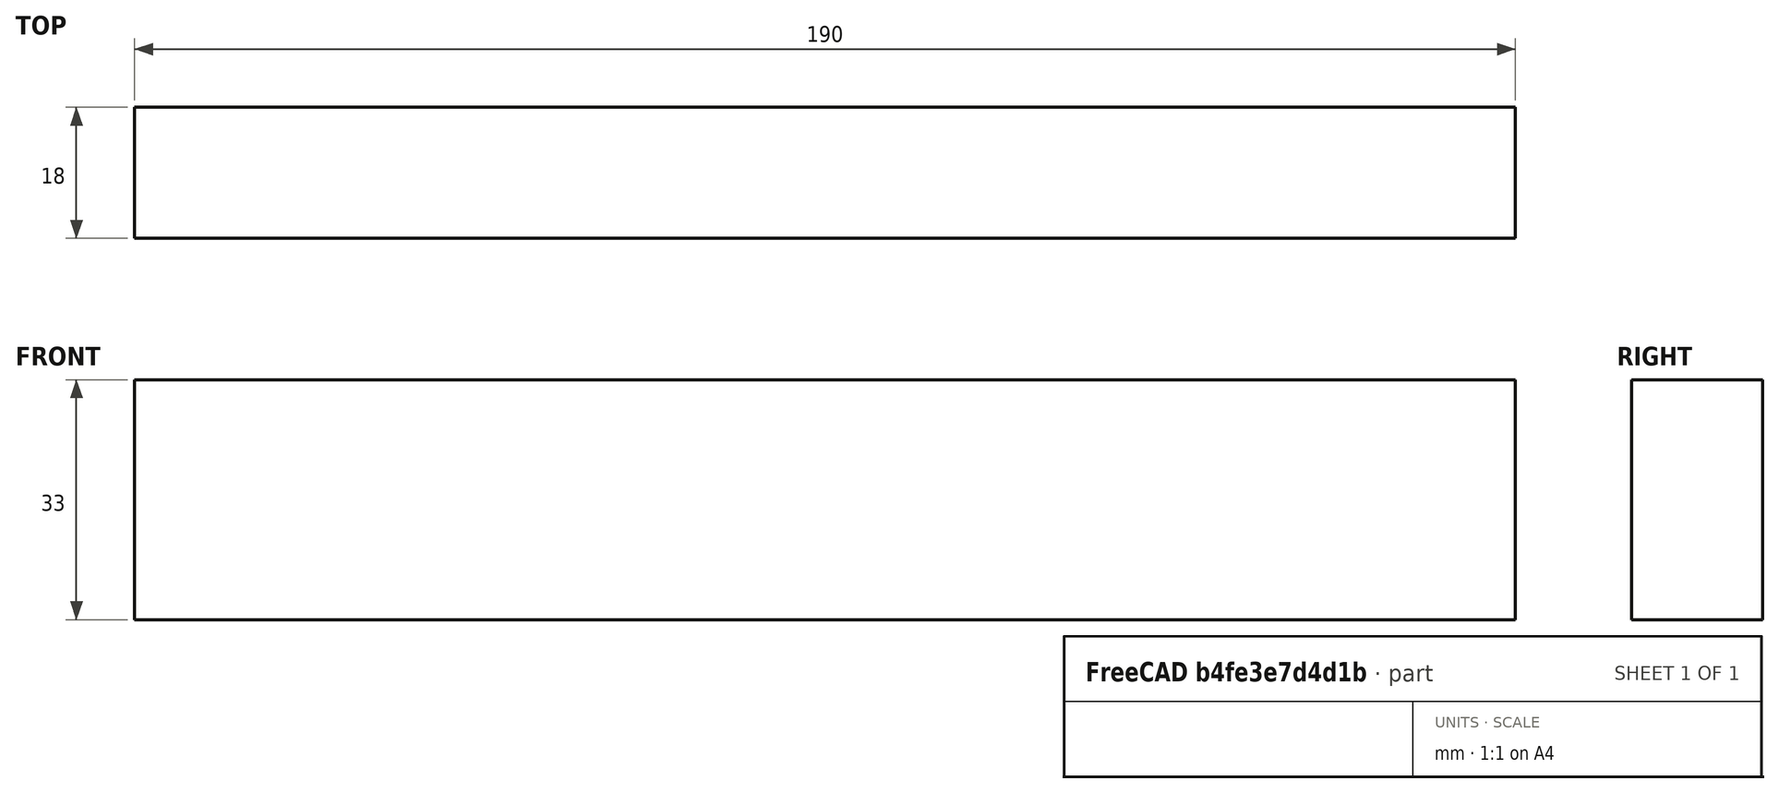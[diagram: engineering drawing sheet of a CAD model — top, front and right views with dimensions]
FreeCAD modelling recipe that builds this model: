
FCSTD DOCUMENT  (FreeCAD 0.18R4 (GitTag))
Label: drawer_back
License: All rights reserved
LicenseURL: http://en.wikipedia.org/wiki/All_rights_reserved
objects: Sketcher::SketchObject×1, PartDesign::Pad×1, PartDesign::Body×1
note: 4 computed .brp shape members not serialized (recipe doc carries the construction recipe); baked Part::Feature solids carry a one-line shape summary decoded from their .brp

FEATURE [Sketcher::SketchObject] Sketch
  MapMode = 5
  Placement = pos=(0,0,0) rot=(1,0,0;1.5708rad)
  Support = -> [XZ_Plane]
  sketch-geometry (4):
    g0: LineSegment StartX=0 StartY=0 StartZ=0 EndX=-190 EndY=0 EndZ=0
    g1: LineSegment StartX=-190 StartY=0 StartZ=0 EndX=-190 EndY=33 EndZ=0
    g2: LineSegment StartX=-190 StartY=33 StartZ=0 EndX=0 EndY=33 EndZ=0
    g3: LineSegment StartX=0 StartY=33 StartZ=0 EndX=0 EndY=0 EndZ=0
  constraints (11):
    c: Coincident(g0,g1)
    c: Coincident(g1,g2)
    c: Coincident(g2,g3)
    c: Coincident(g3,g0)
    c: Horizontal(g0)
    c: Horizontal(g2)
    c: Vertical(g1)
    c: Vertical(g3)
    c: Coincident(g0,g-1)
    c: DistanceY(g3,g3) = 33
    c: DistanceX(g0,g0) = 190
FEATURE [PartDesign::Pad] Pad
  Length = 18
  Length2 = 100
  Placement = pos=(0,0,0) rot=(1,0,0;1.5708rad)
  Profile = -> Sketch
  Type = 0
FEATURE [PartDesign::Body] Body
  Group = -> [Sketch,Pad]
  Origin = -> Origin
  Tip = -> Pad
